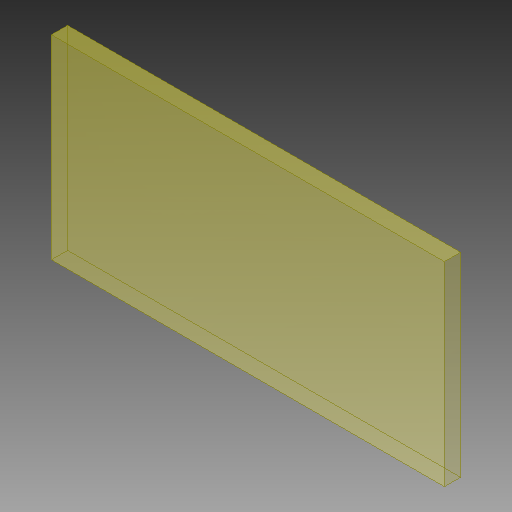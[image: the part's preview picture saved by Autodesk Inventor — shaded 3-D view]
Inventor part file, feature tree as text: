
AUTODESK INVENTOR PART (.ipt)
format: ipt  version: 2018.1 (Build 221171000, 171)  size: 93,696 bytes
history: native  units: mm
features: other x1, extrude x1, sketch x1
ambient origin geometry x8: Origin, YZ Plane, XZ Plane, XY Plane, X Axis, Y Axis, Z Axis, Center Point
bodies: Solid1 (feature_tree)
feature tree (3):
  parser-record x1  (decoder bookkeeping rows leaked as tree rows — omitted from the tree; the rows remain in map.json)
  extrude  "Extrusion1"  Depth=60.0mm
  sketch  "Sketch1"  dims[d0=121.0mm d1=60.0mm d2=5.0mm d3=0.0mm]
note: 1 file-system path scrubbed to <path> (originals preserved in map.json)
